# Revit family: Haworth_Smoke_Table
name_source: partatom
category: Furniture
revit_build: Autodesk Revit 2018 (Build: 20170223_1515(x64)
units: mm (PartAtom-declared; Revit-internal decimal feet)

## family parameters
Always vertical = Yes
Cut with Voids When Loaded = No
OmniClass Number = 23.40.70.14.64.21
OmniClass Title = Systems Furniture
Room Calculation Point = No
Shared = No
Work Plane-Based = No

## types (2) — shared parameters
Actual Height = 17 1/4"
Actual Width = 39 1/4"
Assembly Code = E2020200
Chamfer = 1/16"
Description = Haworth Table Smoke
Manufacturer = Haworth
Model = HCCE-SMK
Product Page URL = https://www.haworth.com
Revision Number = 4
Side Bottom Height = 8 5/16"
Table Edge Finish = Haworth _ Glass _ Clear
Table Finish = Haworth _ Glass _ Smoked
Table Top Thickness = 7/16"
URL = http://www.haworth.com
Warranty = http://www.haworth.com

## per-type parameters (varying)
| type | Actual Depth | Rectangle | Square |
| HCCE-SMK - Square | 39 1/4" | No | Yes |
| HCCE-SMK - Rectangle | 23 3/4" | Yes | No |

## geometry (parser evidence)
native form markers: Sweep x2
no freeform markers — native parametric forms only
